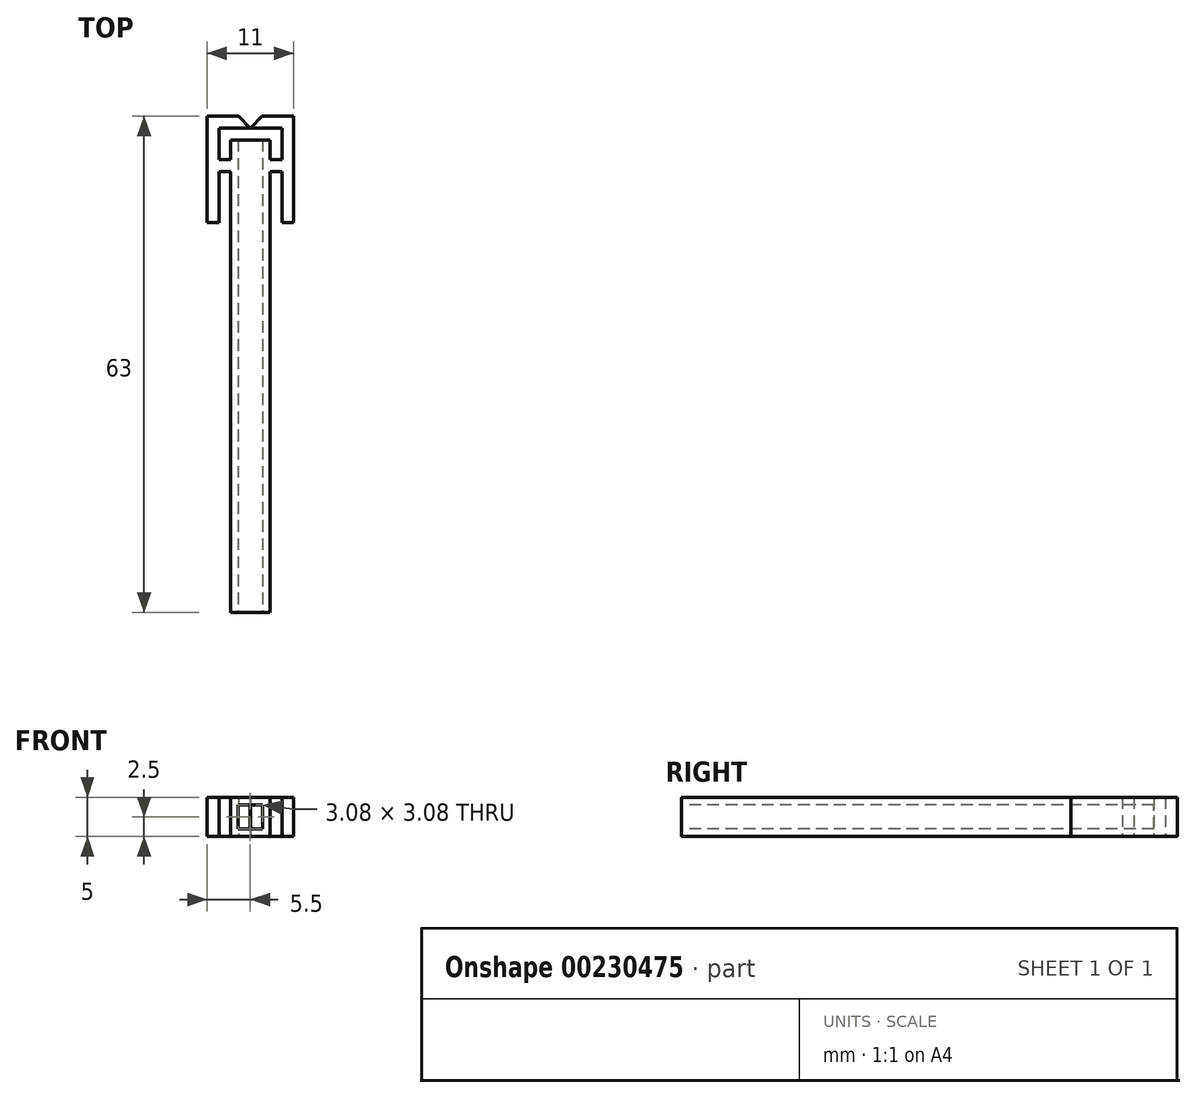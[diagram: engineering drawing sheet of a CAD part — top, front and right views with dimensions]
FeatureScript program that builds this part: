
annotation { "Feature Type Name" : "Feature", "Feature Type Description" : "" }
export const myFeature = defineFeature(function(context is Context, id is Id, definition is map)
    precondition{}
    {
        {
            var Q0;
            Q0=qCreatedBy(makeId("Top.planeOp"),FACE);
            var sketch = newSketch(context, id + "F0", { "sketchPlane" : qUnion([Q0])});
            skLineSegment(sketch, "E0.bottom", {"start": v(1.25, -30) * mm, "end": v(-1.25, -30) * mm});
            skLineSegment(sketch, "E0.top", {"start": v(1.25, 30) * mm, "end": v(-1.25, 30) * mm});
            skLineSegment(sketch, "E0.left", {"start": v(1.25, -30) * mm, "end": v(1.25, 30) * mm});
            skLineSegment(sketch, "E0.right", {"start": v(-1.25, -30) * mm, "end": v(-1.25, 30) * mm});
            skPoint(sketch, "E0.middle", {"position": v(0, 0) * mm});
            skLineSegment(sketch, "E1", {"start": v(1.25, 27.5) * mm, "end": v(2.75, 27.5) * mm});
            skLineSegment(sketch, "E2", {"start": v(2.75, 27.5) * mm, "end": v(2.75, 31.5) * mm});
            skLineSegment(sketch, "E3", {"start": v(-1.23, 31.5) * mm, "end": v(0.27, 33) * mm});
            skLineSegment(sketch, "E4", {"start": v(0.27, 33) * mm, "end": v(4.25, 33) * mm});
            skLineSegment(sketch, "E5", {"start": v(4.25, 33) * mm, "end": v(4.25, 26) * mm});
            skLineSegment(sketch, "E6", {"start": v(4.25, 26) * mm, "end": v(1.25, 26) * mm});
            skLineSegment(sketch, "E7", {"start": v(4.25, 26) * mm, "end": v(4.25, 19.5) * mm});
            skLineSegment(sketch, "E8", {"start": v(4.25, 19.5) * mm, "end": v(2.75, 19.5) * mm});
            skLineSegment(sketch, "E9", {"start": v(2.75, 19.5) * mm, "end": v(2.75, 26) * mm});
            skLineSegment(sketch, "E10", {"start": v(2.75, 31.5) * mm, "end": v(-1.23, 31.5) * mm});
            skSolve(sketch);
        }
        {
            var Q0;
            {var subQ3=sQuery(id+"F0.wireOp",EDGE,"E0.bottom");Q0=makeQuery(id+"F0.imprint","IMPRINT",FACE,{"disambiguationData":[TD([[makeQuery(id+"F0.imprint","IMPRINT",EDGE,{"derivedFrom":subQ3}),-1.0]])]});}
            var Q1;
            {var subQ0=sQuery(id+"F0.wireOp",EDGE,"E1");Q1=makeQuery(id+"F0.imprint","IMPRINT",FACE,{"disambiguationData":[TD([[makeQuery(id+"F0.imprint","IMPRINT",EDGE,{"derivedFrom":subQ0}),-1.0]])]});}
            var Q2;
            {var subQ0=sQuery(id+"F0.wireOp",EDGE,"E7");Q2=makeQuery(id+"F0.imprint","IMPRINT",FACE,{"disambiguationData":[TD([[makeQuery(id+"F0.imprint","IMPRINT",EDGE,{"derivedFrom":subQ0}),-1.0]])]});}
            extrude(context, id + "F1", {"entities" : qUnion([Q0, Q1, Q2]), "depth" : 5 * mm});
        }
        {
            var Q0;
            Q0=makeQuery(id+"F1.opExtrude","SWEPT_BODY",BODY,{"disambiguationData":[OSD([sQuery(id+"F0.wireOp",EDGE,"E0.bottom"),sQuery(id+"F0.wireOp",EDGE,"E0.top"),sQuery(id+"F0.wireOp",EDGE,"E0.left"),sQuery(id+"F0.wireOp",EDGE,"E0.right"),sQuery(id+"F0.wireOp",EDGE,"E1"),sQuery(id+"F0.wireOp",EDGE,"E2"),sQuery(id+"F0.wireOp",EDGE,"yi4CXHjd-efYD-TjNV-R7MP-yIYteb57yjFB"),sQuery(id+"F0.wireOp",EDGE,"E3"),sQuery(id+"F0.wireOp",EDGE,"E4"),sQuery(id+"F0.wireOp",EDGE,"E5"),sQuery(id+"F0.wireOp",EDGE,"E6"),sQuery(id+"F0.wireOp",EDGE,"E7"),sQuery(id+"F0.wireOp",EDGE,"E8"),sQuery(id+"F0.wireOp",EDGE,"E9")])]});
            var Q1;
            Q1=makeQuery(id+"F1.opExtrude","SWEPT_FACE",FACE,{"disambiguationData":[OSD([sQuery(id+"F0.wireOp",EDGE,"E0.right")])]});
            mirror(context, id + "F2", {"operationType" : NewBodyOperationType.ADD, "entities" : qUnion([Q0]), "mirrorPlane" : qUnion([Q1])});
        }
        {
            var Q0;
            {var subQ0=makeQuery(id+"F1.opExtrude","SWEPT_FACE",FACE,{"disambiguationData":[OSD([sQuery(id+"F0.wireOp",EDGE,"E0.bottom")])]});Q0=makeQuery(id+"F2.boolean.opBoolean","MERGE",FACE,{"derivedFrom":[subQ0,makeQuery(id+"F2.opPattern","COPY",FACE,{"derivedFrom":subQ0,"instanceName":"1"})]});}
            var sketch = newSketch(context, id + "F3", { "sketchPlane" : qUnion([Q0])});
            skLineSegment(sketch, "E11.0", {"start": v(-2.8, 0.96) * mm, "end": v(0.29, 0.96) * mm});
            skLineSegment(sketch, "E11.1", {"start": v(-2.8, 4.04) * mm, "end": v(-2.8, 0.96) * mm});
            skLineSegment(sketch, "E11.2", {"start": v(0.29, 4.04) * mm, "end": v(-2.8, 4.04) * mm});
            skLineSegment(sketch, "E11.3", {"start": v(0.29, 0.96) * mm, "end": v(0.29, 4.04) * mm});
            skSolve(sketch);
        }
        {
            var Q0;
            Q0=makeQuery(id+"F3.imprint","IMPRINT",FACE,{"disambiguationData":[TD([[makeQuery(id+"F3.imprint","IMPRINT",EDGE,{"derivedFrom":sQuery(id+"F3.wireOp",EDGE,"E11.0")}),1.0]])]});
            extrude(context, id + "F4", {"entities" : qUnion([Q0]), "operationType" : NewBodyOperationType.REMOVE, "endBound" : BoundingType.UP_TO_NEXT, "oppositeDirection" : true, "depth" : 25 * mm});
        }
    });
